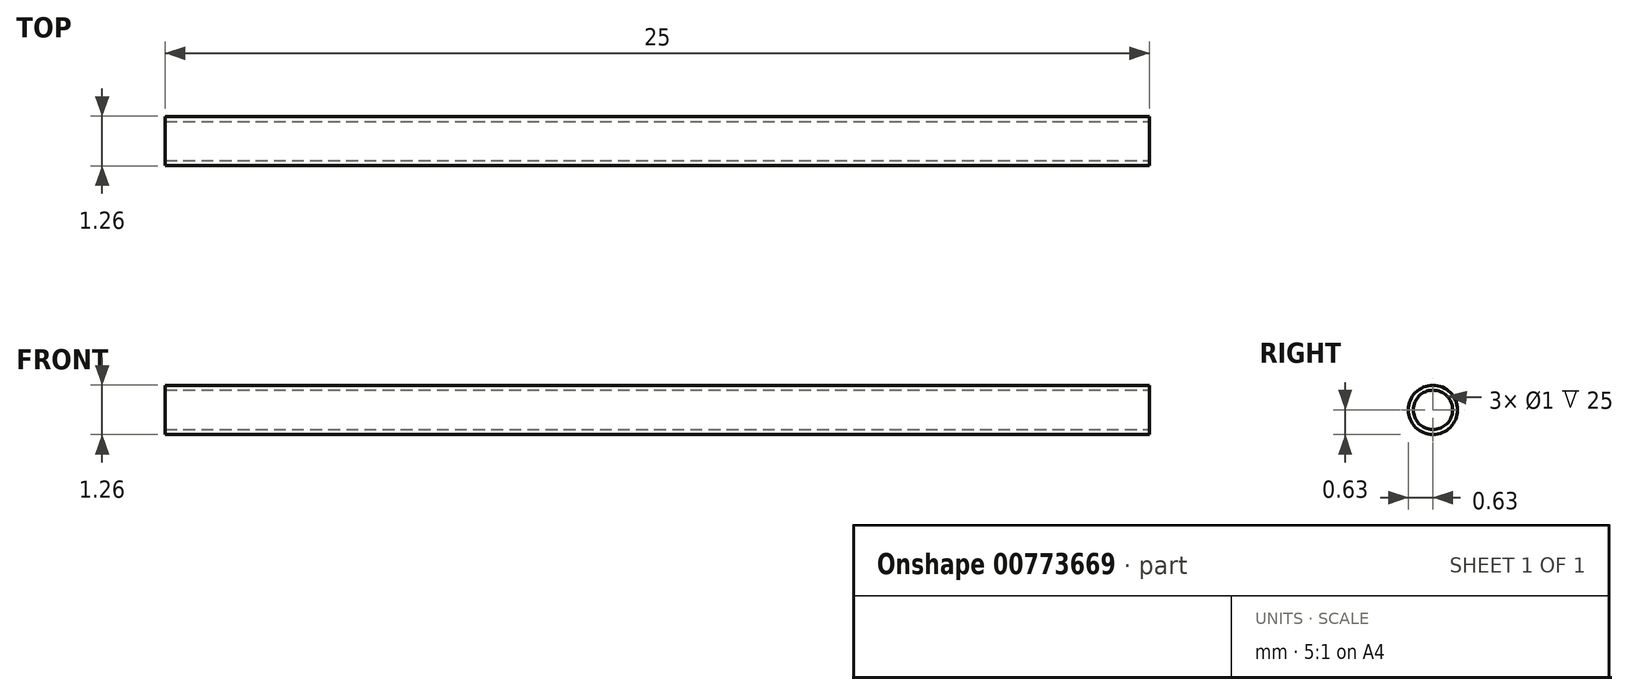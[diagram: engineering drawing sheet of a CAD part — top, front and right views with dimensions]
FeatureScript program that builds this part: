
annotation { "Feature Type Name" : "Feature", "Feature Type Description" : "" }
export const myFeature = defineFeature(function(context is Context, id is Id, definition is map)
    precondition{}
    {
        {
            var Q0;
            Q0=qCreatedBy(makeId("Right.planeOp"),FACE);
            var sketch = newSketch(context, id + "F0", { "sketchPlane" : qUnion([Q0])});
            skCircle(sketch, "E0", {"center": v(0, 0) * mm, "radius": 0.63 * mm});
            skSolve(sketch);
        }
        {
            var Q0;
            Q0 = qSketchRegion(id + "F0", true);
            extrude(context, id + "F1", {"entities" : qUnion([Q0]), "depth" : 25 * mm, "offsetDistance" : 25 * mm});
        }
        {
            var Q0;
            Q0=makeQuery(id+"F1.opExtrude","CAP_FACE",FACE,{"disambiguationData":[OSD([sQuery(id+"F0.wireOp",EDGE,"E0")])],"isStart":false});
            var sketch = newSketch(context, id + "F2", { "sketchPlane" : qUnion([Q0])});
            skPoint(sketch, "E1", {"position": v(0, 0) * mm});
            skSolve(sketch);
        }
        {
            var Q0;
            Q0=sQuery(id+"F2.wireOp",VERTEX,"E1");
            var Q1;
            Q1=makeQuery(id+"F1.opExtrude","SWEPT_BODY",BODY,{"disambiguationData":[OSD([sQuery(id+"F0.wireOp",EDGE,"E0")])]});
            hole(context, id + "F3", {"style" : HoleStyle.SIMPLE, "endStyle" : HoleEndStyle.THROUGH, "holeDiameter" : 1 * mm, "majorDiameter" : 5 * mm, "isTappedThrough" : true, "tappedDepth" : 12 * mm, "tapClearance" : 3, "startFromSketch" : true, "locations" : qUnion([Q0]), "scope" : qUnion([Q1])});
        }
    });
